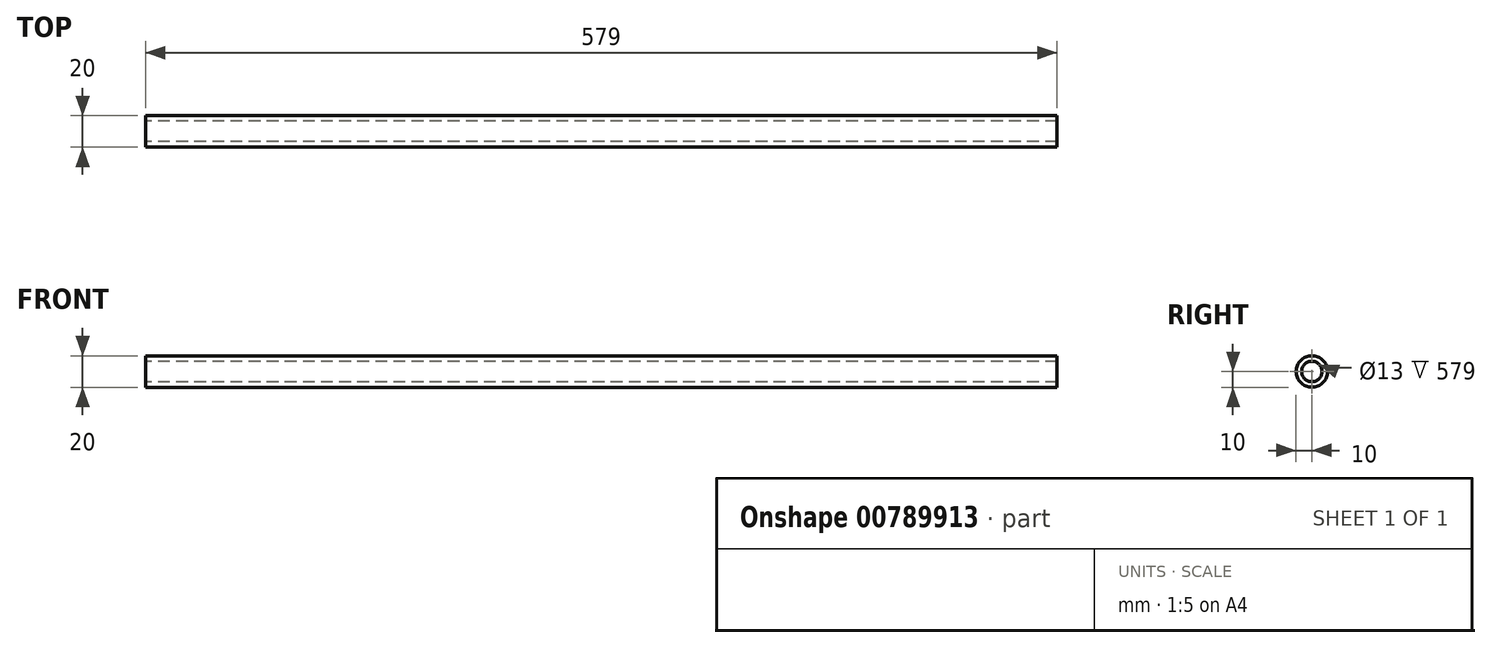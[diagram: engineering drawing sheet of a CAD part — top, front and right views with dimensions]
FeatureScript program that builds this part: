
annotation { "Feature Type Name" : "Feature", "Feature Type Description" : "" }
export const myFeature = defineFeature(function(context is Context, id is Id, definition is map)
    precondition{}
    {
        {
            var Q0;
            Q0=qCreatedBy(makeId("Right.planeOp"),FACE);
            var sketch = newSketch(context, id + "F0", { "sketchPlane" : qUnion([Q0])});
            skCircle(sketch, "E0", {"center": v(0, 0) * mm, "radius": 6.5 * mm});
            skCircle(sketch, "E1", {"center": v(0, 0) * mm, "radius": 10 * mm});
            skSolve(sketch);
        }
        {
            var Q0;
            Q0=qSketchRegion(id+"F0",true);
            extrude(context, id + "F1", {"entities" : qUnion([Q0]), "depth" : 579 * mm, "offsetDistance" : 25 * mm, "symmetric" : true});
        }
    });
